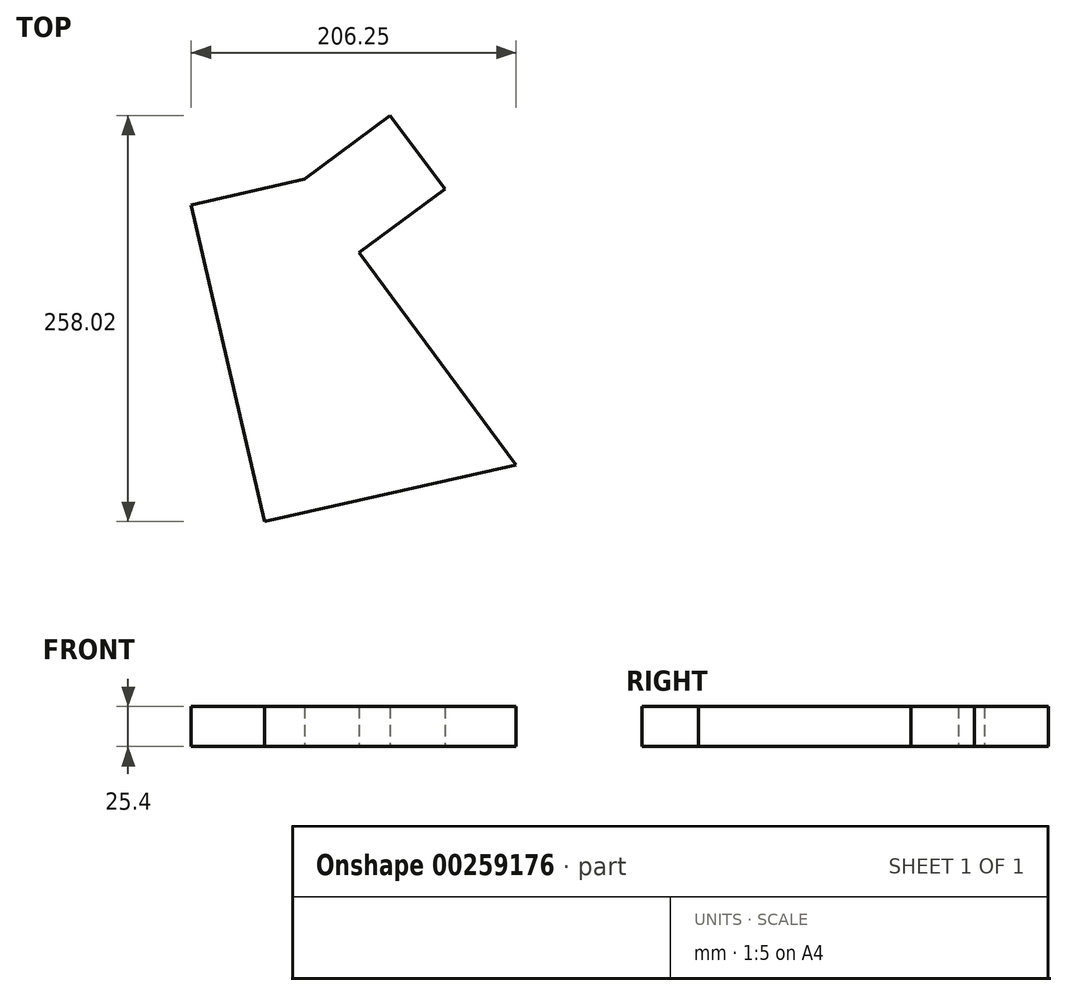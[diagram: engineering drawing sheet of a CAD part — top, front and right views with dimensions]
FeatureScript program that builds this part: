
annotation { "Feature Type Name" : "Feature", "Feature Type Description" : "" }
export const myFeature = defineFeature(function(context is Context, id is Id, definition is map)
    precondition{}
    {
        {
            var Q0;
            Q0=qCreatedBy(makeId("Top.planeOp"),FACE);
            var sketch = newSketch(context, id + "F0", { "sketchPlane" : qUnion([Q0])});
            skLineSegment(sketch, "E0", {"start": v(0, -153.89) * mm, "end": v(-46.67, 47.06) * mm});
            skLineSegment(sketch, "E1", {"start": v(-46.67, 47.06) * mm, "end": v(25.18, 63.75) * mm});
            skLineSegment(sketch, "E2", {"start": v(25.18, 63.75) * mm, "end": v(159.58, -117.9) * mm});
            skLineSegment(sketch, "E3", {"start": v(159.58, -117.9) * mm, "end": v(0, -153.89) * mm});
            skLineSegment(sketch, "E4", {"start": v(25.18, 63.75) * mm, "end": v(79.75, 104.13) * mm});
            skLineSegment(sketch, "E5", {"start": v(79.75, 104.13) * mm, "end": v(114.46, 57.22) * mm});
            skLineSegment(sketch, "E6", {"start": v(114.46, 57.22) * mm, "end": v(52.47, 11.35) * mm});
            skPoint(sketch, "E6.endSnap0", {"position": v(52.47, 83.94) * mm});
            skSolve(sketch);
        }
        {
            var Q0;
            Q0 = qSketchRegion(id + "F0", true);
            extrude(context, id + "F1", {"entities" : qUnion([Q0]), "depth" : 25.4 * mm});
        }
    });
